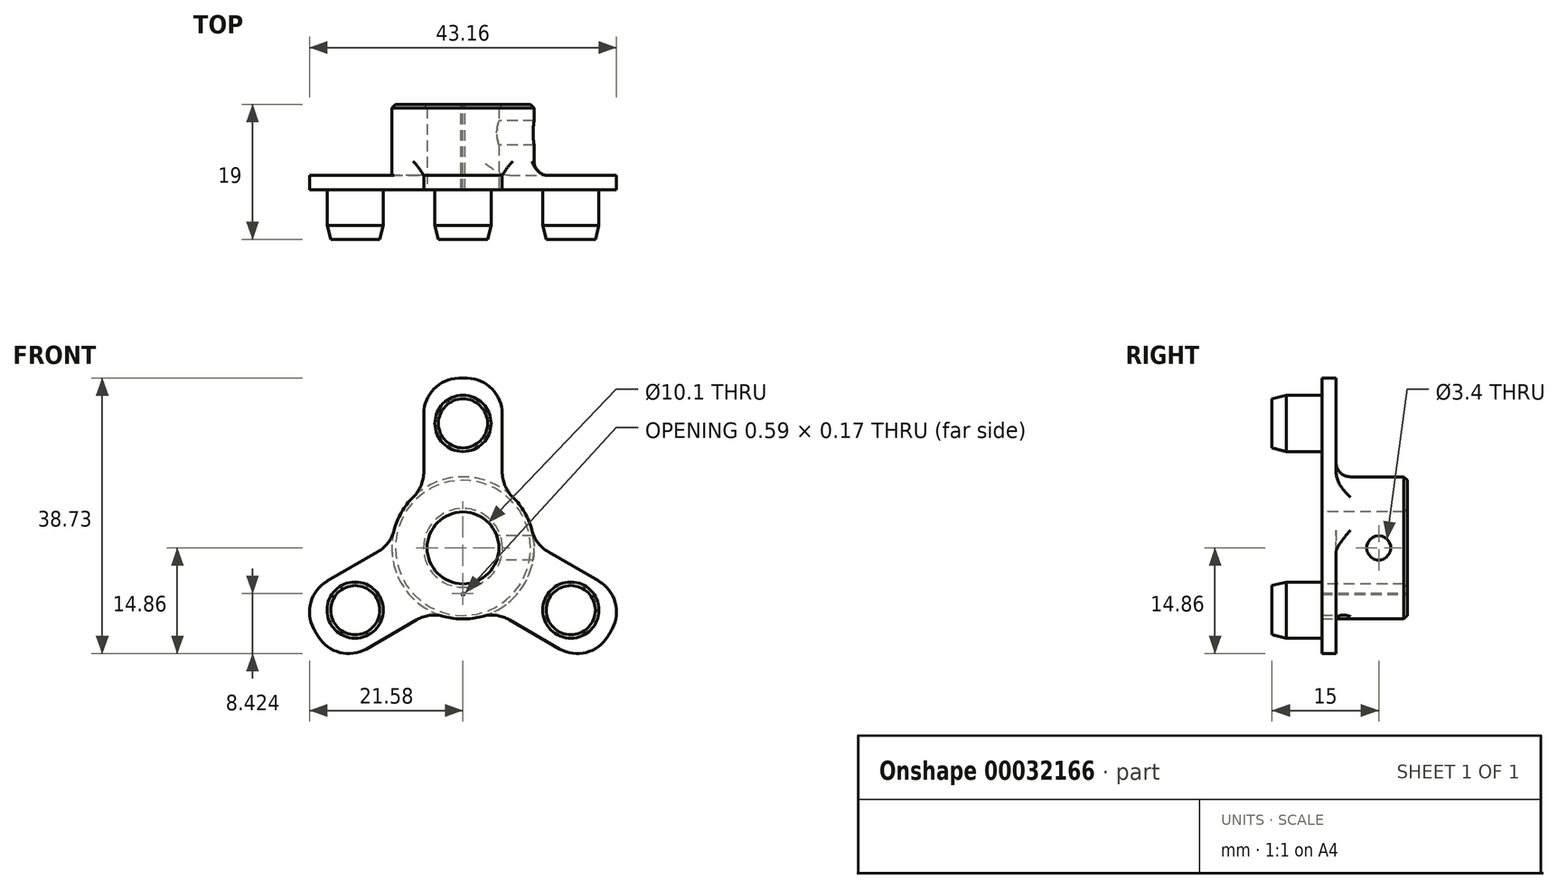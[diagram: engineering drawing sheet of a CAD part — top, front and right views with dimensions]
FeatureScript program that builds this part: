
annotation { "Feature Type Name" : "Feature", "Feature Type Description" : "" }
export const myFeature = defineFeature(function(context is Context, id is Id, definition is map)
    precondition{}
    {
        {
            var Q0;
            Q0=qCreatedBy(makeId("Front.planeOp"),FACE);
            var sketch = newSketch(context, id + "F0", { "sketchPlane" : qUnion([Q0])});
            skCircle(sketch, "E0", {"center": v(0, 17.5) * mm, "radius": 3.95 * mm});
            skCircle(sketch, "E1", {"center": v(15.16, -8.75) * mm, "radius": 3.95 * mm});
            skCircle(sketch, "E2", {"center": v(-15.16, -8.75) * mm, "radius": 3.95 * mm});
            skArc(sketch, "E3", {"start": v(5.5, 23.22) * mm, "mid": v(0, 23.87) * mm, "end": v(-5.5, 23.22) * mm});
            skLineSegment(sketch, "E4.rect.top", {"start": v(0.3, -6.52) * mm, "end": v(-0.3, -6.52) * mm});
            skLineSegment(sketch, "E4.rect.left", {"start": v(5.5, 23.22) * mm, "end": v(5.5, 3.18) * mm});
            skLineSegment(sketch, "E4.rect.right", {"start": v(-5.5, 23.22) * mm, "end": v(-5.5, 3.18) * mm});
            skPoint(sketch, "E4.rect.middle", {"position": v(0, 10.01) * mm});
            skPoint(sketch, "E4.rect.bottom.end.orphan", {"position": v(-5.5, 26.55) * mm});
            skPoint(sketch, "E5.orphan", {"position": v(5.5, 26.55) * mm});
            skLineSegment(sketch, "E6.0", {"start": v(0, -6.35) * mm, "end": v(17.36, -16.37) * mm});
            skLineSegment(sketch, "E7.0", {"start": v(5.5, 3.18) * mm, "end": v(22.86, -6.85) * mm});
            skLineSegment(sketch, "E8.0", {"start": v(-5.5, 3.18) * mm, "end": v(-22.86, -6.85) * mm});
            skLineSegment(sketch, "E9.0", {"start": v(0, -6.35) * mm, "end": v(-17.36, -16.37) * mm});
            skPoint(sketch, "E10.orphan", {"position": v(-5.5, -6.52) * mm});
            skPoint(sketch, "E11.orphan", {"position": v(5.5, -6.52) * mm});
            skArc(sketch, "E12.trimOffspring", {"start": v(-22.86, -6.85) * mm, "mid": v(-20.67, -11.93) * mm, "end": v(-17.36, -16.37) * mm});
            skArc(sketch, "E13.trimOffspring", {"start": v(17.36, -16.37) * mm, "mid": v(20.67, -11.93) * mm, "end": v(22.86, -6.85) * mm});
            skCircle(sketch, "E14", {"center": v(0, 0) * mm, "radius": 5.05 * mm});
            skCircle(sketch, "E15", {"center": v(0, 0) * mm, "radius": 10 * mm});
            skSolve(sketch);
        }
        {
            var Q0;
            Q0=makeQuery(id+"F0.imprint","IMPRINT",FACE,{"disambiguationData":[TD([[makeQuery(id+"F0.imprint","IMPRINT",EDGE,{"derivedFrom":sQuery(id+"F0.wireOp",EDGE,"E0")}),-1.0]])]});
            var Q1;
            Q1=makeQuery(id+"F0.imprint","IMPRINT",FACE,{"disambiguationData":[TD([[makeQuery(id+"F0.imprint","IMPRINT",EDGE,{"derivedFrom":sQuery(id+"F0.wireOp",EDGE,"E0")}),1.0]])]});
            var Q2;
            Q2=makeQuery(id+"F0.imprint","IMPRINT",FACE,{"disambiguationData":[TD([[makeQuery(id+"F0.imprint","IMPRINT",EDGE,{"derivedFrom":sQuery(id+"F0.wireOp",EDGE,"E2")}),1.0]])]});
            var Q3;
            Q3=makeQuery(id+"F0.imprint","IMPRINT",FACE,{"disambiguationData":[TD([[makeQuery(id+"F0.imprint","IMPRINT",EDGE,{"derivedFrom":sQuery(id+"F0.wireOp",EDGE,"E1")}),1.0]])]});
            var Q4;
            Q4=makeQuery(id+"F0.imprint","IMPRINT",FACE,{"disambiguationData":[TD([[makeQuery(id+"F0.imprint","IMPRINT",EDGE,{"derivedFrom":sQuery(id+"F0.wireOp",EDGE,"E14")}),1.0]])]});
            var Q5;
            Q5=makeQuery(id+"F0.imprint","IMPRINT",FACE,{"disambiguationData":[TD([[makeQuery(id+"F0.imprint","IMPRINT",EDGE,{"derivedFrom":sQuery(id+"F0.wireOp",EDGE,"E14")}),-1.0]])]});
            var Q6;
            {var subQ1=sQuery(id+"F0.wireOp",EDGE,"E8.0");var subQ3=sQuery(id+"F0.wireOp",EDGE,"E4.rect.right");var subQ5=makeQuery(id+"F0.imprint","INTERSECT",VERTEX,{"derivedFrom":[subQ3,subQ1]});Q6=makeQuery(id+"F0.imprint","IMPRINT",FACE,{"disambiguationData":[TD([[makeQuery(id+"F0.imprint","IMPRINT",EDGE,{"disambiguationData":[TD([[subQ5,1.0]])],"derivedFrom":subQ3}),-1.0]])]});}
            var Q7;
            Q7=makeQuery(id+"F0.imprint","IMPRINT",FACE,{"disambiguationData":[TD([[makeQuery(id+"F0.imprint","IMPRINT",EDGE,{"derivedFrom":sQuery(id+"F0.wireOp",EDGE,"E2")}),-1.0]])]});
            var Q8;
            Q8=makeQuery(id+"F0.imprint","IMPRINT",FACE,{"disambiguationData":[TD([[makeQuery(id+"F0.imprint","IMPRINT",EDGE,{"derivedFrom":sQuery(id+"F0.wireOp",EDGE,"E1")}),-1.0]])]});
            var Q9;
            {var subQ1=sQuery(id+"F0.wireOp",EDGE,"E7.0");var subQ3=sQuery(id+"F0.wireOp",EDGE,"E4.rect.left");var subQ5=makeQuery(id+"F0.imprint","INTERSECT",VERTEX,{"derivedFrom":[subQ3,subQ1]});Q9=makeQuery(id+"F0.imprint","IMPRINT",FACE,{"disambiguationData":[TD([[makeQuery(id+"F0.imprint","IMPRINT",EDGE,{"disambiguationData":[TD([[subQ5,1.0]])],"derivedFrom":subQ3}),1.0]])]});}
            var Q10;
            {var subQ5=sQuery(id+"F0.wireOp",EDGE,"E4.rect.top");Q10=makeQuery(id+"F0.imprint","IMPRINT",FACE,{"disambiguationData":[TD([[makeQuery(id+"F0.imprint","IMPRINT",EDGE,{"derivedFrom":subQ5}),1.0]])]});}
            extrude(context, id + "F1", {"entities" : qUnion([Q0, Q1, Q2, Q3, Q4, Q5, Q6, Q7, Q8, Q9, Q10]), "depth" : 2 * mm});
        }
        {
            var Q0;
            Q0=makeQuery(id+"F0.imprint","IMPRINT",FACE,{"disambiguationData":[TD([[makeQuery(id+"F0.imprint","IMPRINT",EDGE,{"derivedFrom":sQuery(id+"F0.wireOp",EDGE,"E0")}),1.0]])]});
            var Q1;
            Q1=makeQuery(id+"F0.imprint","IMPRINT",FACE,{"disambiguationData":[TD([[makeQuery(id+"F0.imprint","IMPRINT",EDGE,{"derivedFrom":sQuery(id+"F0.wireOp",EDGE,"E2")}),1.0]])]});
            var Q2;
            Q2=makeQuery(id+"F0.imprint","IMPRINT",FACE,{"disambiguationData":[TD([[makeQuery(id+"F0.imprint","IMPRINT",EDGE,{"derivedFrom":sQuery(id+"F0.wireOp",EDGE,"E1")}),1.0]])]});
            extrude(context, id + "F2", {"entities" : qUnion([Q0, Q1, Q2]), "operationType" : NewBodyOperationType.ADD, "depth" : 9 * mm});
        }
        {
            var Q0;
            Q0=makeQuery(id+"F1.opExtrude","SWEPT_EDGE",EDGE,{"disambiguationData":[OSD([sQuery(id+"F0.wireOp",EDGE,"E3"),sQuery(id+"F0.wireOp",EDGE,"E4.rect.right")])]});
            var Q1;
            Q1=makeQuery(id+"F1.opExtrude","SWEPT_EDGE",EDGE,{"disambiguationData":[OSD([sQuery(id+"F0.wireOp",EDGE,"E8.0"),sQuery(id+"F0.wireOp",EDGE,"E12.trimOffspring")])]});
            var Q2;
            Q2=makeQuery(id+"F1.opExtrude","SWEPT_EDGE",EDGE,{"disambiguationData":[OSD([sQuery(id+"F0.wireOp",EDGE,"E3"),sQuery(id+"F0.wireOp",EDGE,"E4.rect.right")])]});
            var Q3;
            Q3=makeQuery(id+"F1.opExtrude","SWEPT_EDGE",EDGE,{"disambiguationData":[OSD([sQuery(id+"F0.wireOp",EDGE,"E3"),sQuery(id+"F0.wireOp",EDGE,"E4.rect.left")])]});
            var Q4;
            Q4=makeQuery(id+"F1.opExtrude","SWEPT_EDGE",EDGE,{"disambiguationData":[OSD([sQuery(id+"F0.wireOp",EDGE,"E8.0"),sQuery(id+"F0.wireOp",EDGE,"E12.trimOffspring")])]});
            var Q5;
            Q5=makeQuery(id+"F1.opExtrude","SWEPT_EDGE",EDGE,{"disambiguationData":[OSD([sQuery(id+"F0.wireOp",EDGE,"E6.0"),sQuery(id+"F0.wireOp",EDGE,"E13.trimOffspring")])]});
            var Q6;
            Q6=makeQuery(id+"F1.opExtrude","SWEPT_EDGE",EDGE,{"disambiguationData":[OSD([sQuery(id+"F0.wireOp",EDGE,"E7.0"),sQuery(id+"F0.wireOp",EDGE,"E13.trimOffspring")])]});
            var Q7;
            Q7=makeQuery(id+"F1.opExtrude","SWEPT_EDGE",EDGE,{"disambiguationData":[OSD([sQuery(id+"F0.wireOp",EDGE,"E3"),sQuery(id+"F0.wireOp",EDGE,"E4.rect.left")])]});
            var Q8;
            Q8=makeQuery(id+"F1.opExtrude","SWEPT_EDGE",EDGE,{"disambiguationData":[OSD([sQuery(id+"F0.wireOp",EDGE,"E7.0"),sQuery(id+"F0.wireOp",EDGE,"E13.trimOffspring")])]});
            var Q9;
            Q9=makeQuery(id+"F1.opExtrude","SWEPT_EDGE",EDGE,{"disambiguationData":[OSD([sQuery(id+"F0.wireOp",EDGE,"E9.0"),sQuery(id+"F0.wireOp",EDGE,"E12.trimOffspring")])]});
            fillet(context, id + "F3", {"entities" : qUnion([Q0, Q1, Q2, Q3, Q4, Q5, Q6, Q7, Q8, Q9]), "radius" : 5 * mm, "tangentPropagation" : true, "allowEdgeOverflow" : false});
        }
        {
            var Q0;
            Q0=makeQuery(id+"F2.opExtrude","CAP_EDGE",EDGE,{"disambiguationData":[OSD([sQuery(id+"F0.wireOp",EDGE,"E0")])],"isStart":false});
            var Q1;
            Q1=makeQuery(id+"F2.opExtrude","CAP_FACE",FACE,{"disambiguationData":[OSD([sQuery(id+"F0.wireOp",EDGE,"E2")])],"isStart":false});
            var Q2;
            Q2=makeQuery(id+"F2.opExtrude","CAP_FACE",FACE,{"disambiguationData":[OSD([sQuery(id+"F0.wireOp",EDGE,"E1")])],"isStart":false});
            var Q3;
            Q3=makeQuery(id+"F2.opExtrude","CAP_EDGE",EDGE,{"disambiguationData":[OSD([sQuery(id+"F0.wireOp",EDGE,"E14")])],"isStart":false});
            chamfer(context, id + "F4", {"entities" : qUnion([Q0, Q1, Q2, Q3]), "chamferType" : ChamferType.TWO_OFFSETS, "width1" : .5 * mm, "oppositeDirection" : false, "width2" : 2 * mm, "tangentPropagation" : true});
        }
        {
            var Q0;
            {var subQ5=sQuery(id+"F0.wireOp",EDGE,"E4.rect.top");Q0=makeQuery(id+"F0.imprint","IMPRINT",FACE,{"disambiguationData":[TD([[makeQuery(id+"F0.imprint","IMPRINT",EDGE,{"derivedFrom":subQ5}),1.0]])]});}
            var Q1;
            Q1=makeQuery(id+"F0.imprint","IMPRINT",FACE,{"disambiguationData":[TD([[makeQuery(id+"F0.imprint","IMPRINT",EDGE,{"derivedFrom":sQuery(id+"F0.wireOp",EDGE,"E14")}),-1.0]])]});
            var Q2;
            {var subQ1=sQuery(id+"F0.wireOp",EDGE,"E8.0");var subQ3=sQuery(id+"F0.wireOp",EDGE,"E4.rect.right");var subQ5=makeQuery(id+"F0.imprint","INTERSECT",VERTEX,{"derivedFrom":[subQ3,subQ1]});Q2=makeQuery(id+"F0.imprint","IMPRINT",FACE,{"disambiguationData":[TD([[makeQuery(id+"F0.imprint","IMPRINT",EDGE,{"disambiguationData":[TD([[subQ5,1.0]])],"derivedFrom":subQ3}),-1.0]])]});}
            var Q3;
            {var subQ1=sQuery(id+"F0.wireOp",EDGE,"E7.0");var subQ3=sQuery(id+"F0.wireOp",EDGE,"E4.rect.left");var subQ5=makeQuery(id+"F0.imprint","INTERSECT",VERTEX,{"derivedFrom":[subQ3,subQ1]});Q3=makeQuery(id+"F0.imprint","IMPRINT",FACE,{"disambiguationData":[TD([[makeQuery(id+"F0.imprint","IMPRINT",EDGE,{"disambiguationData":[TD([[subQ5,1.0]])],"derivedFrom":subQ3}),1.0]])]});}
            extrude(context, id + "F5", {"entities" : qUnion([Q0, Q1, Q2, Q3]), "operationType" : NewBodyOperationType.ADD, "oppositeDirection" : true, "depth" : 10 * mm});
        }
        {
            var Q0;
            Q0=makeQuery(id+"F0.imprint","IMPRINT",FACE,{"disambiguationData":[TD([[makeQuery(id+"F0.imprint","IMPRINT",EDGE,{"derivedFrom":sQuery(id+"F0.wireOp",EDGE,"E14")}),1.0]])]});
            extrude(context, id + "F6", {"entities" : qUnion([Q0]), "operationType" : NewBodyOperationType.REMOVE, "endBound" : BoundingType.UP_TO_NEXT, "depth" : 25 * mm});
        }
        {
            var Q0;
            {var subQ0=sQuery(id+"F0.wireOp",EDGE,"E15");var subQ6=sQuery(id+"F0.wireOp",EDGE,"E4.rect.left");Q0=makeQuery(id+"F5.boolean.opBoolean","SPLIT",EDGE,{"disambiguationData":[TD([makeQuery(id+"F1.opExtrude","SWEPT_FACE",FACE,{"disambiguationData":[OSD([subQ6])]})])],"derivedFrom":makeQuery(id+"F5.opExtrude","CAP_EDGE",EDGE,{"disambiguationData":[OSD([subQ0])],"isStart":true})});}
            var Q1;
            {var subQ0=sQuery(id+"F0.wireOp",EDGE,"E15");var subQ1=sQuery(id+"F0.wireOp",EDGE,"E8.0");Q1=makeQuery(id+"F5.boolean.opBoolean","SPLIT",EDGE,{"disambiguationData":[TD([makeQuery(id+"F1.opExtrude","SWEPT_FACE",FACE,{"disambiguationData":[OSD([subQ1])]})])],"derivedFrom":makeQuery(id+"F5.opExtrude","CAP_EDGE",EDGE,{"disambiguationData":[OSD([subQ0])],"isStart":true})});}
            var Q2;
            {var subQ0=sQuery(id+"F0.wireOp",EDGE,"E15");var subQ6=sQuery(id+"F0.wireOp",EDGE,"E7.0");Q2=makeQuery(id+"F5.boolean.opBoolean","SPLIT",EDGE,{"disambiguationData":[TD([makeQuery(id+"F1.opExtrude","SWEPT_FACE",FACE,{"disambiguationData":[OSD([subQ6])]})])],"derivedFrom":makeQuery(id+"F5.opExtrude","CAP_EDGE",EDGE,{"disambiguationData":[OSD([subQ0])],"isStart":true})});}
            fillet(context, id + "F7", {"entities" : qUnion([Q0, Q1, Q2]), "radius" : 2 * mm, "tangentPropagation" : true, "allowEdgeOverflow" : false});
        }
        {
            var Q0;
            Q0=qCreatedBy(makeId("Right.planeOp"),FACE);
            var sketch = newSketch(context, id + "F8", { "sketchPlane" : qUnion([Q0])});
            skLineSegment(sketch, "E16.0", {"start": v(10, -10) * mm, "end": v(10, 10) * mm});
            skLineSegment(sketch, "E17.0", {"start": v(2, 8.35) * mm, "end": v(2, 10) * mm});
            skPoint(sketch, "E18.0", {"position": v(2, -8.94) * mm});
            skLineSegment(sketch, "E19.0", {"start": v(10, -5.05) * mm, "end": v(10, 5.05) * mm});
            skLineSegment(sketch, "E20", {"start": v(2, 8.35) * mm, "end": v(2, -8.94) * mm, "construction": true});
            skLineSegment(sketch, "E21", {"start": v(2, 0) * mm, "end": v(10, 0) * mm, "construction": true});
            skLineSegment(sketch, "E22", {"start": v(6, 0) * mm, "end": v(6, -1.07) * mm, "construction": true});
            skCircle(sketch, "E23", {"center": v(6, 0) * mm, "radius": 1.7 * mm});
            skSolve(sketch);
        }
        {
            var Q0;
            Q0=makeQuery(id+"F8.imprint","IMPRINT",FACE,{"disambiguationData":[TD([[makeQuery(id+"F8.imprint","IMPRINT",EDGE,{"derivedFrom":sQuery(id+"F8.wireOp",EDGE,"E23")}),1.0]])]});
            var Q1;
            Q1=sQuery(id+"F8.wireOp",EDGE,"E23");
            extrude(context, id + "F9", {"entities" : qUnion([Q0]), "operationType" : NewBodyOperationType.REMOVE, "surfaceEntities" : qUnion([Q1]), "endBound" : BoundingType.THROUGH_ALL, "depth" : 25 * mm});
        }
        {
            var Q0;
            Q0=makeQuery(id+"F5.opExtrude","CAP_EDGE",EDGE,{"disambiguationData":[OSD([sQuery(id+"F0.wireOp",EDGE,"E15")])],"isStart":false});
            var Q1;
            Q1=makeQuery(id+"F5.opExtrude","CAP_EDGE",EDGE,{"disambiguationData":[OSD([sQuery(id+"F0.wireOp",EDGE,"E14")])],"isStart":false});
            var Q2;
            Q2=makeQuery(id+"F6.boolean.opBoolean","COPY",EDGE,{"derivedFrom":makeQuery(id+"F6.opExtrude","TWEAK_EDGE",EDGE,{"derivedFrom":[makeQuery(id+"F0.imprint","IMPRINT",EDGE,{"derivedFrom":sQuery(id+"F0.wireOp",EDGE,"E14")}),makeQuery(id+"F1.opExtrude","CAP_FACE",FACE,{"disambiguationData":[OSD([sQuery(id+"F0.wireOp",EDGE,"E3"),sQuery(id+"F0.wireOp",EDGE,"E4.rect.top"),sQuery(id+"F0.wireOp",EDGE,"E4.rect.left"),sQuery(id+"F0.wireOp",EDGE,"E4.rect.right"),sQuery(id+"F0.wireOp",EDGE,"E6.0"),sQuery(id+"F0.wireOp",EDGE,"E7.0"),sQuery(id+"F0.wireOp",EDGE,"E8.0"),sQuery(id+"F0.wireOp",EDGE,"E9.0"),sQuery(id+"F0.wireOp",EDGE,"E12.trimOffspring"),sQuery(id+"F0.wireOp",EDGE,"E13.trimOffspring"),sQuery(id+"F0.wireOp",EDGE,"E15")])],"isStart":false})]})});
            chamfer(context, id + "F10", {"entities" : qUnion([Q0, Q1, Q2]), "width" : .5 * mm, "tangentPropagation" : true});
        }
        {
            var Q0;
            Q0=makeQuery(id+"F1.opExtrude","SWEPT_EDGE",EDGE,{"disambiguationData":[OSD([sQuery(id+"F0.wireOp",EDGE,"E4.rect.right"),sQuery(id+"F0.wireOp",EDGE,"E15")])]});
            var Q1;
            Q1=makeQuery(id+"F1.opExtrude","SWEPT_EDGE",EDGE,{"disambiguationData":[OSD([sQuery(id+"F0.wireOp",EDGE,"E8.0"),sQuery(id+"F0.wireOp",EDGE,"E15")])]});
            var Q2;
            Q2=makeQuery(id+"F1.opExtrude","SWEPT_EDGE",EDGE,{"disambiguationData":[OSD([sQuery(id+"F0.wireOp",EDGE,"E4.rect.left"),sQuery(id+"F0.wireOp",EDGE,"E15")])]});
            var Q3;
            Q3=makeQuery(id+"F1.opExtrude","SWEPT_EDGE",EDGE,{"disambiguationData":[OSD([sQuery(id+"F0.wireOp",EDGE,"E7.0"),sQuery(id+"F0.wireOp",EDGE,"E15")])]});
            var Q4;
            Q4=makeQuery(id+"F1.opExtrude","SWEPT_EDGE",EDGE,{"disambiguationData":[OSD([sQuery(id+"F0.wireOp",EDGE,"E6.0"),sQuery(id+"F0.wireOp",EDGE,"E15")])]});
            var Q5;
            Q5=makeQuery(id+"F1.opExtrude","SWEPT_EDGE",EDGE,{"disambiguationData":[OSD([sQuery(id+"F0.wireOp",EDGE,"E9.0"),sQuery(id+"F0.wireOp",EDGE,"E15")])]});
            fillet(context, id + "F11", {"entities" : qUnion([Q0, Q1, Q2, Q3, Q4, Q5]), "radius" : 5 * mm, "tangentPropagation" : true, "allowEdgeOverflow" : false});
        }
    });
